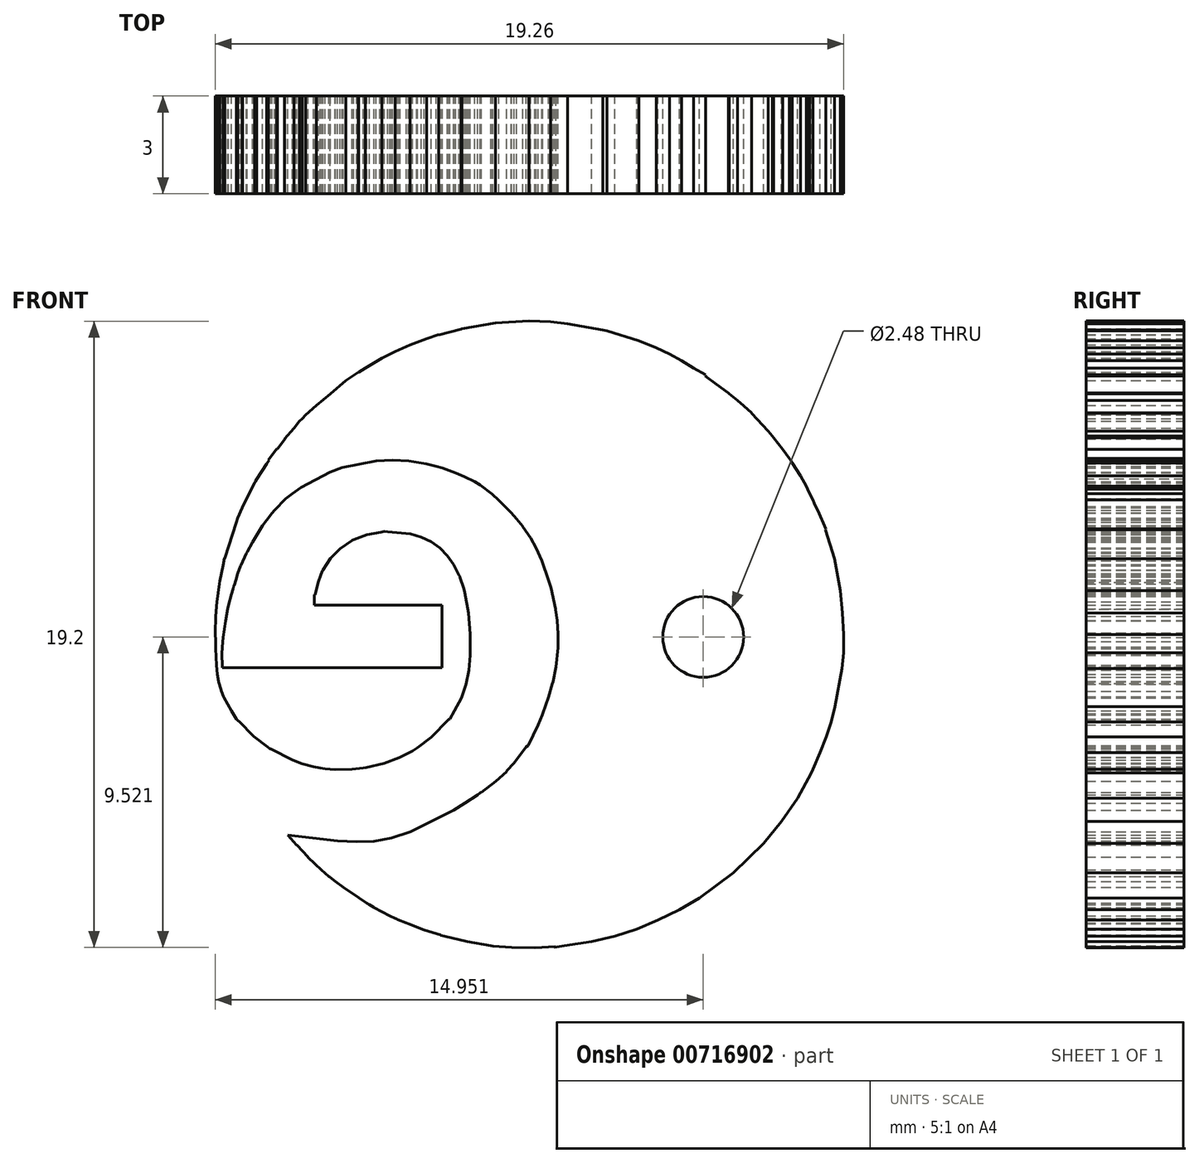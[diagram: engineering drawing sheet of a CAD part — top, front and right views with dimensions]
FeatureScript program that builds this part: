
annotation { "Feature Type Name" : "Feature", "Feature Type Description" : "" }
export const myFeature = defineFeature(function(context is Context, id is Id, definition is map)
    precondition{}
    {
        {
            var Q0;
            Q0=qCreatedBy(makeId("Front.planeOp"),FACE);
            var sketch = newSketch(context, id + "F0", { "sketchPlane" : qUnion([Q0])});
            skCircle(sketch, "E0", {"center": v(5.32, -0.08) * mm, "radius": 1.24 * mm});
            skLineSegment(sketch, "E1", {"start": v(7.48, 6.03) * mm, "end": v(7.76, 5.67) * mm});
            skLineSegment(sketch, "E2", {"start": v(7.76, 5.67) * mm, "end": v(7.96, 5.39) * mm});
            skLineSegment(sketch, "E3", {"start": v(7.44, 6.07) * mm, "end": v(7.48, 6.03) * mm});
            skLineSegment(sketch, "E4", {"start": v(7.44, 6.07) * mm, "end": v(7.44, 6.08) * mm});
            skLineSegment(sketch, "E5", {"start": v(7.44, 6.08) * mm, "end": v(7.3, 6.23) * mm});
            skLineSegment(sketch, "E6", {"start": v(6.8, 6.77) * mm, "end": v(7.3, 6.23) * mm});
            skLineSegment(sketch, "E7", {"start": v(6.8, 6.77) * mm, "end": v(6.8, 6.79) * mm});
            skLineSegment(sketch, "E8", {"start": v(6.8, 6.79) * mm, "end": v(6.57, 7) * mm});
            skLineSegment(sketch, "E9", {"start": v(6.12, 7.38) * mm, "end": v(6.37, 7.17) * mm});
            skLineSegment(sketch, "E10", {"start": v(6.37, 7.17) * mm, "end": v(6.57, 7) * mm});
            skLineSegment(sketch, "E11", {"start": v(6.1, 7.4) * mm, "end": v(6.12, 7.38) * mm});
            skLineSegment(sketch, "E12", {"start": v(6.1, 7.4) * mm, "end": v(6.1, 7.4) * mm});
            skLineSegment(sketch, "E13", {"start": v(6.1, 7.4) * mm, "end": v(5.72, 7.67) * mm});
            skLineSegment(sketch, "E14", {"start": v(5.39, 7.92) * mm, "end": v(5.72, 7.67) * mm});
            skLineSegment(sketch, "E15", {"start": v(5.39, 7.92) * mm, "end": v(5.4, 7.96) * mm});
            skLineSegment(sketch, "E16", {"start": v(5.4, 7.96) * mm, "end": v(5.03, 8.16) * mm});
            skLineSegment(sketch, "E17", {"start": v(4.66, 8.38) * mm, "end": v(5.03, 8.16) * mm});
            skLineSegment(sketch, "E18", {"start": v(4.66, 8.38) * mm, "end": v(4.66, 8.39) * mm});
            skLineSegment(sketch, "E19", {"start": v(4.66, 8.39) * mm, "end": v(4.3, 8.59) * mm});
            skLineSegment(sketch, "E20", {"start": v(4.3, 8.59) * mm, "end": v(4.3, 8.59) * mm});
            skLineSegment(sketch, "E21", {"start": v(3.35, 9) * mm, "end": v(3.88, 8.78) * mm});
            skLineSegment(sketch, "E22", {"start": v(3.88, 8.78) * mm, "end": v(4.3, 8.59) * mm});
            skLineSegment(sketch, "E23", {"start": v(2.37, 9.3) * mm, "end": v(3.35, 9) * mm});
            skLineSegment(sketch, "E24", {"start": v(2.37, 9.3) * mm, "end": v(2.37, 9.3) * mm});
            skLineSegment(sketch, "E25", {"start": v(2.37, 9.3) * mm, "end": v(2.25, 9.33) * mm});
            skLineSegment(sketch, "E26", {"start": v(1.17, 9.52) * mm, "end": v(2.25, 9.33) * mm});
            skLineSegment(sketch, "E27", {"start": v(-0.02, 9.6) * mm, "end": v(0.65, 9.58) * mm});
            skLineSegment(sketch, "E28", {"start": v(0.65, 9.58) * mm, "end": v(1.17, 9.52) * mm});
            skLineSegment(sketch, "E29", {"start": v(-2.07, 9.37) * mm, "end": v(-1.04, 9.55) * mm});
            skLineSegment(sketch, "E30", {"start": v(-1.04, 9.55) * mm, "end": v(-0.02, 9.6) * mm});
            skLineSegment(sketch, "E31", {"start": v(-2.07, 9.37) * mm, "end": v(-2.07, 9.37) * mm});
            skLineSegment(sketch, "E32", {"start": v(-2.07, 9.37) * mm, "end": v(-2.1, 9.36) * mm});
            skLineSegment(sketch, "E33", {"start": v(-2.78, 9.18) * mm, "end": v(-2.1, 9.36) * mm});
            skLineSegment(sketch, "E34", {"start": v(-2.78, 9.18) * mm, "end": v(-2.78, 9.18) * mm});
            skLineSegment(sketch, "E35", {"start": v(-2.78, 9.18) * mm, "end": v(-3.15, 9.06) * mm});
            skLineSegment(sketch, "E36", {"start": v(-4.12, 8.67) * mm, "end": v(-3.66, 8.87) * mm});
            skLineSegment(sketch, "E37", {"start": v(-3.66, 8.87) * mm, "end": v(-3.15, 9.06) * mm});
            skLineSegment(sketch, "E38", {"start": v(-5.03, 8.16) * mm, "end": v(-4.53, 8.46) * mm});
            skLineSegment(sketch, "E39", {"start": v(-4.53, 8.46) * mm, "end": v(-4.12, 8.67) * mm});
            skLineSegment(sketch, "E40", {"start": v(-5.03, 8.16) * mm, "end": v(-5.24, 8.04) * mm});
            skLineSegment(sketch, "E41", {"start": v(-5.24, 8.04) * mm, "end": v(-5.24, 8.03) * mm});
            skLineSegment(sketch, "E42", {"start": v(-5.62, 7.77) * mm, "end": v(-5.24, 8.03) * mm});
            skLineSegment(sketch, "E43", {"start": v(-5.62, 7.77) * mm, "end": v(-6.1, 7.38) * mm});
            skLineSegment(sketch, "E44", {"start": v(-6.1, 7.38) * mm, "end": v(-6.53, 7.02) * mm});
            skLineSegment(sketch, "E45", {"start": v(-6.53, 7.02) * mm, "end": v(-6.86, 6.72) * mm});
            skLineSegment(sketch, "E46", {"start": v(-6.86, 6.72) * mm, "end": v(-6.97, 6.62) * mm});
            skLineSegment(sketch, "E47", {"start": v(-6.97, 6.62) * mm, "end": v(-7.05, 6.53) * mm});
            skLineSegment(sketch, "E48", {"start": v(-7.05, 6.53) * mm, "end": v(-7.22, 6.32) * mm});
            skLineSegment(sketch, "E49", {"start": v(-7.22, 6.32) * mm, "end": v(-7.5, 6) * mm});
            skLineSegment(sketch, "E50", {"start": v(-7.5, 6) * mm, "end": v(-7.48, 6) * mm});
            skLineSegment(sketch, "E51", {"start": v(-7.48, 6) * mm, "end": v(-7.72, 5.69) * mm});
            skLineSegment(sketch, "E52", {"start": v(-7.72, 5.69) * mm, "end": v(-7.75, 5.69) * mm});
            skLineSegment(sketch, "E53", {"start": v(-7.75, 5.69) * mm, "end": v(-8, 5.34) * mm});
            skLineSegment(sketch, "E54", {"start": v(-8, 5.34) * mm, "end": v(-7.97, 5.34) * mm});
            skLineSegment(sketch, "E55", {"start": v(-7.97, 5.34) * mm, "end": v(-8, 5.3) * mm});
            skLineSegment(sketch, "E56", {"start": v(-8, 5.3) * mm, "end": v(-8.05, 5.23) * mm});
            skLineSegment(sketch, "E57", {"start": v(-8.05, 5.23) * mm, "end": v(-8.36, 4.75) * mm});
            skLineSegment(sketch, "E58", {"start": v(-8.36, 4.75) * mm, "end": v(-8.4, 4.69) * mm});
            skLineSegment(sketch, "E59", {"start": v(-8.4, 4.69) * mm, "end": v(-8.42, 4.64) * mm});
            skLineSegment(sketch, "E60", {"start": v(-8.42, 4.64) * mm, "end": v(-8.42, 4.64) * mm});
            skLineSegment(sketch, "E61", {"start": v(-8.42, 4.64) * mm, "end": v(-8.78, 3.92) * mm});
            skLineSegment(sketch, "E62", {"start": v(-8.78, 3.92) * mm, "end": v(-8.79, 3.92) * mm});
            skLineSegment(sketch, "E63", {"start": v(-8.79, 3.92) * mm, "end": v(-8.8, 3.89) * mm});
            skLineSegment(sketch, "E64", {"start": v(-8.8, 3.89) * mm, "end": v(-8.94, 3.56) * mm});
            skLineSegment(sketch, "E65", {"start": v(-8.94, 3.56) * mm, "end": v(-8.98, 3.44) * mm});
            skLineSegment(sketch, "E66", {"start": v(-8.98, 3.44) * mm, "end": v(-9.33, 2.33) * mm});
            skLineSegment(sketch, "E67", {"start": v(-9.33, 2.33) * mm, "end": v(-9.35, 2.33) * mm});
            skLineSegment(sketch, "E68", {"start": v(-9.35, 2.33) * mm, "end": v(-9.38, 2.11) * mm});
            skLineSegment(sketch, "E69", {"start": v(-9.38, 2.11) * mm, "end": v(-9.48, 1.64) * mm});
            skLineSegment(sketch, "E70", {"start": v(-9.48, 1.64) * mm, "end": v(-9.49, 1.64) * mm});
            skLineSegment(sketch, "E71", {"start": v(-9.49, 1.64) * mm, "end": v(-9.5, 1.55) * mm});
            skLineSegment(sketch, "E72", {"start": v(-9.5, 1.55) * mm, "end": v(-9.58, 1) * mm});
            skLineSegment(sketch, "E73", {"start": v(-9.58, 1) * mm, "end": v(-9.61, 0.55) * mm});
            skLineSegment(sketch, "E74", {"start": v(-9.61, 0.55) * mm, "end": v(-9.63, 0.05) * mm});
            skLineSegment(sketch, "E75", {"start": v(-9.63, 0.05) * mm, "end": v(-9.62, -0.23) * mm});
            skLineSegment(sketch, "E76", {"start": v(-9.62, -0.23) * mm, "end": v(-9.62, -0.44) * mm});
            skLineSegment(sketch, "E77", {"start": v(-9.62, -0.44) * mm, "end": v(-9.62, -0.44) * mm});
            skLineSegment(sketch, "E78", {"start": v(-9.62, -0.44) * mm, "end": v(-9.6, -0.94) * mm});
            skLineSegment(sketch, "E79", {"start": v(-9.6, -0.94) * mm, "end": v(-9.57, -1.23) * mm});
            skLineSegment(sketch, "E80", {"start": v(-9.57, -1.23) * mm, "end": v(-9.53, -1.45) * mm});
            skLineSegment(sketch, "E81", {"start": v(-9.53, -1.45) * mm, "end": v(-9.53, -1.45) * mm});
            skLineSegment(sketch, "E82", {"start": v(-9.53, -1.45) * mm, "end": v(-9.5, -1.53) * mm});
            skLineSegment(sketch, "E83", {"start": v(-9.5, -1.53) * mm, "end": v(-9.44, -1.74) * mm});
            skLineSegment(sketch, "E84", {"start": v(-9.44, -1.74) * mm, "end": v(-9.37, -1.9) * mm});
            skLineSegment(sketch, "E85", {"start": v(-9.37, -1.9) * mm, "end": v(-9.36, -1.93) * mm});
            skLineSegment(sketch, "E86", {"start": v(-9.36, -1.93) * mm, "end": v(-9.13, -2.35) * mm});
            skLineSegment(sketch, "E87", {"start": v(-9.13, -2.35) * mm, "end": v(-8.98, -2.6) * mm});
            skLineSegment(sketch, "E88", {"start": v(-8.98, -2.6) * mm, "end": v(-8.92, -2.66) * mm});
            skLineSegment(sketch, "E89", {"start": v(-8.92, -2.66) * mm, "end": v(-8.9, -2.66) * mm});
            skLineSegment(sketch, "E90", {"start": v(-8.9, -2.66) * mm, "end": v(-8.45, -3.14) * mm});
            skLineSegment(sketch, "E91", {"start": v(-8.45, -3.14) * mm, "end": v(-8.03, -3.45) * mm});
            skLineSegment(sketch, "E92", {"start": v(-8.03, -3.45) * mm, "end": v(-7.96, -3.5) * mm});
            skLineSegment(sketch, "E93", {"start": v(-7.96, -3.5) * mm, "end": v(-7.94, -3.51) * mm});
            skLineSegment(sketch, "E94", {"start": v(-7.94, -3.51) * mm, "end": v(-7.93, -3.51) * mm});
            skLineSegment(sketch, "E95", {"start": v(-7.93, -3.51) * mm, "end": v(-7.26, -3.86) * mm});
            skLineSegment(sketch, "E96", {"start": v(-7.26, -3.86) * mm, "end": v(-6.96, -3.97) * mm});
            skLineSegment(sketch, "E97", {"start": v(-6.96, -3.97) * mm, "end": v(-6.62, -4.06) * mm});
            skLineSegment(sketch, "E98", {"start": v(-6.62, -4.06) * mm, "end": v(-6.41, -4.1) * mm});
            skLineSegment(sketch, "E99", {"start": v(-6.41, -4.1) * mm, "end": v(-6.26, -4.12) * mm});
            skLineSegment(sketch, "E100", {"start": v(-6.26, -4.12) * mm, "end": v(-5.96, -4.15) * mm});
            skLineSegment(sketch, "E101", {"start": v(-5.96, -4.15) * mm, "end": v(-5.44, -4.14) * mm});
            skLineSegment(sketch, "E102", {"start": v(-5.44, -4.14) * mm, "end": v(-5.1, -4.1) * mm});
            skLineSegment(sketch, "E103", {"start": v(-5.1, -4.1) * mm, "end": v(-5, -4.08) * mm});
            skLineSegment(sketch, "E104", {"start": v(-5, -4.08) * mm, "end": v(-4.46, -3.96) * mm});
            skLineSegment(sketch, "E105", {"start": v(-4.46, -3.96) * mm, "end": v(-3.99, -3.78) * mm});
            skLineSegment(sketch, "E106", {"start": v(-3.99, -3.78) * mm, "end": v(-3.96, -3.77) * mm});
            skLineSegment(sketch, "E107", {"start": v(-3.96, -3.77) * mm, "end": v(-3.61, -3.6) * mm});
            skLineSegment(sketch, "E108", {"start": v(-3.61, -3.6) * mm, "end": v(-3.59, -3.58) * mm});
            skLineSegment(sketch, "E109", {"start": v(-3.59, -3.58) * mm, "end": v(-3.43, -3.48) * mm});
            skLineSegment(sketch, "E110", {"start": v(-3.43, -3.48) * mm, "end": v(-3, -3.16) * mm});
            skLineSegment(sketch, "E111", {"start": v(-3, -3.16) * mm, "end": v(-2.48, -2.6) * mm});
            skLineSegment(sketch, "E112", {"start": v(-2.48, -2.6) * mm, "end": v(-2.44, -2.6) * mm});
            skLineSegment(sketch, "E113", {"start": v(-2.44, -2.6) * mm, "end": v(-2.3, -2.35) * mm});
            skLineSegment(sketch, "E114", {"start": v(-2.3, -2.35) * mm, "end": v(-2.08, -1.95) * mm});
            skLineSegment(sketch, "E115", {"start": v(-2.08, -1.95) * mm, "end": v(-1.94, -1.53) * mm});
            skLineSegment(sketch, "E116", {"start": v(-1.94, -1.53) * mm, "end": v(-1.86, -1.1) * mm});
            skLineSegment(sketch, "E117", {"start": v(-1.86, -1.1) * mm, "end": v(-1.82, -0.64) * mm});
            skLineSegment(sketch, "E118", {"start": v(-1.82, -0.64) * mm, "end": v(-1.81, 0) * mm});
            skLineSegment(sketch, "E119", {"start": v(-1.81, 0) * mm, "end": v(-1.86, 0.65) * mm});
            skLineSegment(sketch, "E120", {"start": v(-1.86, 0.65) * mm, "end": v(-1.98, 1.28) * mm});
            skLineSegment(sketch, "E121", {"start": v(-1.98, 1.28) * mm, "end": v(-2, 1.4) * mm});
            skLineSegment(sketch, "E122", {"start": v(-2, 1.4) * mm, "end": v(-2.01, 1.39) * mm});
            skLineSegment(sketch, "E123", {"start": v(-2.01, 1.39) * mm, "end": v(-2.13, 1.76) * mm});
            skLineSegment(sketch, "E124", {"start": v(-2.13, 1.76) * mm, "end": v(-2.13, 1.76) * mm});
            skLineSegment(sketch, "E125", {"start": v(-2.13, 1.76) * mm, "end": v(-2.16, 1.81) * mm});
            skLineSegment(sketch, "E126", {"start": v(-2.16, 1.81) * mm, "end": v(-2.32, 2.14) * mm});
            skLineSegment(sketch, "E127", {"start": v(-2.32, 2.14) * mm, "end": v(-2.51, 2.41) * mm});
            skLineSegment(sketch, "E128", {"start": v(-2.51, 2.41) * mm, "end": v(-2.74, 2.65) * mm});
            skLineSegment(sketch, "E129", {"start": v(-2.74, 2.65) * mm, "end": v(-3.01, 2.84) * mm});
            skLineSegment(sketch, "E130", {"start": v(-3.01, 2.84) * mm, "end": v(-3.3, 2.98) * mm});
            skLineSegment(sketch, "E131", {"start": v(-3.3, 2.98) * mm, "end": v(-3.64, 3.08) * mm});
            skLineSegment(sketch, "E132", {"start": v(-3.64, 3.08) * mm, "end": v(-4.35, 3.15) * mm});
            skLineSegment(sketch, "E133", {"start": v(-4.35, 3.15) * mm, "end": v(-4.45, 3.15) * mm});
            skLineSegment(sketch, "E134", {"start": v(-4.45, 3.15) * mm, "end": v(-4.55, 3.14) * mm});
            skLineSegment(sketch, "E135", {"start": v(-4.55, 3.14) * mm, "end": v(-4.99, 3.05) * mm});
            skLineSegment(sketch, "E136", {"start": v(-4.99, 3.05) * mm, "end": v(-5.39, 2.9) * mm});
            skLineSegment(sketch, "E137", {"start": v(-5.39, 2.9) * mm, "end": v(-5.42, 2.89) * mm});
            skLineSegment(sketch, "E138", {"start": v(-5.42, 2.89) * mm, "end": v(-5.44, 2.87) * mm});
            skLineSegment(sketch, "E139", {"start": v(-5.44, 2.87) * mm, "end": v(-5.8, 2.62) * mm});
            skLineSegment(sketch, "E140", {"start": v(-5.8, 2.62) * mm, "end": v(-6.1, 2.33) * mm});
            skLineSegment(sketch, "E141", {"start": v(-6.1, 2.33) * mm, "end": v(-6.32, 1.97) * mm});
            skLineSegment(sketch, "E142", {"start": v(-6.32, 1.97) * mm, "end": v(-6.34, 1.97) * mm});
            skLineSegment(sketch, "E143", {"start": v(-6.34, 1.97) * mm, "end": v(-6.39, 1.84) * mm});
            skLineSegment(sketch, "E144", {"start": v(-6.39, 1.84) * mm, "end": v(-6.48, 1.58) * mm});
            skLineSegment(sketch, "E145", {"start": v(-6.48, 1.58) * mm, "end": v(-6.48, 1.58) * mm});
            skLineSegment(sketch, "E146", {"start": v(-6.48, 1.58) * mm, "end": v(-6.56, 1.21) * mm});
            skLineSegment(sketch, "E147", {"start": v(-6.56, 1.21) * mm, "end": v(-6.59, 1.2) * mm});
            skLineSegment(sketch, "E148", {"start": v(-6.59, 1.2) * mm, "end": v(-6.59, 0.9) * mm});
            skLineSegment(sketch, "E149", {"start": v(-6.59, 0.9) * mm, "end": v(-2.68, 0.9) * mm});
            skLineSegment(sketch, "E150", {"start": v(-2.68, 0.9) * mm, "end": v(-2.68, -1.02) * mm});
            skLineSegment(sketch, "E151", {"start": v(-2.87, -1.02) * mm, "end": v(-2.68, -1.02) * mm});
            skLineSegment(sketch, "E152", {"start": v(-2.87, -1.02) * mm, "end": v(-3.46, -1.02) * mm});
            skLineSegment(sketch, "E153", {"start": v(-3.46, -1.02) * mm, "end": v(-3.46, -1.02) * mm});
            skLineSegment(sketch, "E154", {"start": v(-4.59, -1.02) * mm, "end": v(-3.46, -1.02) * mm});
            skLineSegment(sketch, "E155", {"start": v(-4.59, -1.02) * mm, "end": v(-4.58, -1.02) * mm});
            skLineSegment(sketch, "E156", {"start": v(-4.58, -1.02) * mm, "end": v(-9.4, -1.02) * mm});
            skLineSegment(sketch, "E157", {"start": v(-9.4, -0.98) * mm, "end": v(-9.43, -0.6) * mm});
            skLineSegment(sketch, "E158", {"start": v(-9.38, -0.1) * mm, "end": v(-9.41, -0.38) * mm});
            skLineSegment(sketch, "E159", {"start": v(-9.41, -0.38) * mm, "end": v(-9.43, -0.6) * mm});
            skLineSegment(sketch, "E160", {"start": v(-9.31, 0.41) * mm, "end": v(-9.38, -0.1) * mm});
            skLineSegment(sketch, "E161", {"start": v(-9.31, 0.41) * mm, "end": v(-9.3, 0.41) * mm});
            skLineSegment(sketch, "E162", {"start": v(-9.3, 0.41) * mm, "end": v(-9.24, 0.78) * mm});
            skLineSegment(sketch, "E163", {"start": v(-9.22, 0.9) * mm, "end": v(-9.24, 0.78) * mm});
            skLineSegment(sketch, "E164", {"start": v(-9.13, 1.23) * mm, "end": v(-9.22, 0.9) * mm});
            skLineSegment(sketch, "E165", {"start": v(-9.09, 1.39) * mm, "end": v(-9.13, 1.23) * mm});
            skLineSegment(sketch, "E166", {"start": v(-9.08, 1.41) * mm, "end": v(-9.09, 1.39) * mm});
            skLineSegment(sketch, "E167", {"start": v(-9.07, 1.43) * mm, "end": v(-9.08, 1.41) * mm});
            skLineSegment(sketch, "E168", {"start": v(-9.05, 1.5) * mm, "end": v(-9.07, 1.43) * mm});
            skLineSegment(sketch, "E169", {"start": v(-9.05, 1.5) * mm, "end": v(-9.05, 1.5) * mm});
            skLineSegment(sketch, "E170", {"start": v(-9, 1.67) * mm, "end": v(-9.05, 1.5) * mm});
            skLineSegment(sketch, "E171", {"start": v(-8.85, 2.1) * mm, "end": v(-8.94, 1.86) * mm});
            skLineSegment(sketch, "E172", {"start": v(-8.94, 1.86) * mm, "end": v(-9, 1.67) * mm});
            skLineSegment(sketch, "E173", {"start": v(-8.85, 2.11) * mm, "end": v(-8.85, 2.1) * mm});
            skLineSegment(sketch, "E174", {"start": v(-8.68, 2.48) * mm, "end": v(-8.85, 2.11) * mm});
            skLineSegment(sketch, "E175", {"start": v(-8.66, 2.52) * mm, "end": v(-8.68, 2.48) * mm});
            skLineSegment(sketch, "E176", {"start": v(-8.66, 2.52) * mm, "end": v(-8.49, 2.82) * mm});
            skLineSegment(sketch, "E177", {"start": v(-8.17, 3.33) * mm, "end": v(-8.49, 2.82) * mm});
            skLineSegment(sketch, "E178", {"start": v(-7.89, 3.72) * mm, "end": v(-8.05, 3.5) * mm});
            skLineSegment(sketch, "E179", {"start": v(-8.05, 3.5) * mm, "end": v(-8.17, 3.33) * mm});
            skLineSegment(sketch, "E180", {"start": v(-7.82, 3.8) * mm, "end": v(-7.89, 3.72) * mm});
            skLineSegment(sketch, "E181", {"start": v(-7.82, 3.8) * mm, "end": v(-7.81, 3.8) * mm});
            skLineSegment(sketch, "E182", {"start": v(-7.81, 3.8) * mm, "end": v(-7.47, 4.15) * mm});
            skLineSegment(sketch, "E183", {"start": v(-7, 4.5) * mm, "end": v(-7.26, 4.31) * mm});
            skLineSegment(sketch, "E184", {"start": v(-7.26, 4.31) * mm, "end": v(-7.47, 4.15) * mm});
            skLineSegment(sketch, "E185", {"start": v(-7, 4.5) * mm, "end": v(-6.12, 4.97) * mm});
            skLineSegment(sketch, "E186", {"start": v(-5.74, 5.1) * mm, "end": v(-6.12, 4.97) * mm});
            skLineSegment(sketch, "E187", {"start": v(-5.74, 5.1) * mm, "end": v(-4.7, 5.32) * mm});
            skLineSegment(sketch, "E188", {"start": v(-4.2, 5.35) * mm, "end": v(-4.7, 5.32) * mm});
            skLineSegment(sketch, "E189", {"start": v(-4.2, 5.35) * mm, "end": v(-4.2, 5.34) * mm});
            skLineSegment(sketch, "E190", {"start": v(-4.2, 5.34) * mm, "end": v(-3.7, 5.32) * mm});
            skLineSegment(sketch, "E191", {"start": v(-3.17, 5.23) * mm, "end": v(-3.7, 5.32) * mm});
            skLineSegment(sketch, "E192", {"start": v(-3.17, 5.23) * mm, "end": v(-2.86, 5.15) * mm});
            skLineSegment(sketch, "E193", {"start": v(-2.26, 4.95) * mm, "end": v(-2.66, 5.1) * mm});
            skLineSegment(sketch, "E194", {"start": v(-2.66, 5.1) * mm, "end": v(-2.86, 5.15) * mm});
            skLineSegment(sketch, "E195", {"start": v(-1.67, 4.68) * mm, "end": v(-2, 4.84) * mm});
            skLineSegment(sketch, "E196", {"start": v(-2, 4.84) * mm, "end": v(-2.26, 4.95) * mm});
            skLineSegment(sketch, "E197", {"start": v(-1.67, 4.68) * mm, "end": v(-1.51, 4.58) * mm});
            skLineSegment(sketch, "E198", {"start": v(-1.14, 4.3) * mm, "end": v(-1.51, 4.58) * mm});
            skLineSegment(sketch, "E199", {"start": v(-1.14, 4.3) * mm, "end": v(-0.94, 4.11) * mm});
            skLineSegment(sketch, "E200", {"start": v(-0.56, 3.72) * mm, "end": v(-0.94, 4.11) * mm});
            skLineSegment(sketch, "E201", {"start": v(-0.2, 3.3) * mm, "end": v(-0.4, 3.54) * mm});
            skLineSegment(sketch, "E202", {"start": v(-0.4, 3.54) * mm, "end": v(-0.56, 3.72) * mm});
            skLineSegment(sketch, "E203", {"start": v(-0.2, 3.3) * mm, "end": v(-0.2, 3.3) * mm});
            skLineSegment(sketch, "E204", {"start": v(-0.2, 3.3) * mm, "end": v(0.04, 2.95) * mm});
            skLineSegment(sketch, "E205", {"start": v(0.38, 2.25) * mm, "end": v(0.2, 2.65) * mm});
            skLineSegment(sketch, "E206", {"start": v(0.2, 2.65) * mm, "end": v(0.04, 2.95) * mm});
            skLineSegment(sketch, "E207", {"start": v(0.59, 1.66) * mm, "end": v(0.38, 2.25) * mm});
            skLineSegment(sketch, "E208", {"start": v(0.65, 1.43) * mm, "end": v(0.59, 1.66) * mm});
            skLineSegment(sketch, "E209", {"start": v(0.8, 0.78) * mm, "end": v(0.65, 1.43) * mm});
            skLineSegment(sketch, "E210", {"start": v(0.8, 0.78) * mm, "end": v(0.8, 0.78) * mm});
            skLineSegment(sketch, "E211", {"start": v(0.8, 0.75) * mm, "end": v(0.8, 0.78) * mm});
            skLineSegment(sketch, "E212", {"start": v(0.88, 0.01) * mm, "end": v(0.84, 0.43) * mm});
            skLineSegment(sketch, "E213", {"start": v(0.84, 0.43) * mm, "end": v(0.8, 0.75) * mm});
            skLineSegment(sketch, "E214", {"start": v(0.88, 0.01) * mm, "end": v(0.88, -0.41) * mm});
            skLineSegment(sketch, "E215", {"start": v(0.82, -1) * mm, "end": v(0.88, -0.41) * mm});
            skLineSegment(sketch, "E216", {"start": v(0.82, -1) * mm, "end": v(0.72, -1.45) * mm});
            skLineSegment(sketch, "E217", {"start": v(0.7, -1.52) * mm, "end": v(0.72, -1.45) * mm});
            skLineSegment(sketch, "E218", {"start": v(0.4, -2.43) * mm, "end": v(0.58, -1.93) * mm});
            skLineSegment(sketch, "E219", {"start": v(0.58, -1.93) * mm, "end": v(0.7, -1.52) * mm});
            skLineSegment(sketch, "E220", {"start": v(0.4, -2.46) * mm, "end": v(0.4, -2.43) * mm});
            skLineSegment(sketch, "E221", {"start": v(0.4, -2.46) * mm, "end": v(0.26, -2.78) * mm});
            skLineSegment(sketch, "E222", {"start": v(-0.04, -3.4) * mm, "end": v(0.26, -2.78) * mm});
            skLineSegment(sketch, "E223", {"start": v(-0.04, -3.4) * mm, "end": v(-0.1, -3.45) * mm});
            skLineSegment(sketch, "E224", {"start": v(-0.1, -3.45) * mm, "end": v(-0.47, -3.94) * mm});
            skLineSegment(sketch, "E225", {"start": v(-0.47, -3.94) * mm, "end": v(-0.7, -4.2) * mm});
            skLineSegment(sketch, "E226", {"start": v(-0.7, -4.2) * mm, "end": v(-0.7, -4.21) * mm});
            skLineSegment(sketch, "E227", {"start": v(-1.48, -4.84) * mm, "end": v(-1.03, -4.5) * mm});
            skLineSegment(sketch, "E228", {"start": v(-1.03, -4.5) * mm, "end": v(-0.7, -4.21) * mm});
            skLineSegment(sketch, "E229", {"start": v(-1.49, -4.84) * mm, "end": v(-1.48, -4.84) * mm});
            skLineSegment(sketch, "E230", {"start": v(-1.5, -4.86) * mm, "end": v(-1.49, -4.84) * mm});
            skLineSegment(sketch, "E231", {"start": v(-1.51, -4.86) * mm, "end": v(-1.5, -4.86) * mm});
            skLineSegment(sketch, "E232", {"start": v(-1.6, -4.92) * mm, "end": v(-1.51, -4.86) * mm});
            skLineSegment(sketch, "E233", {"start": v(-1.99, -5.18) * mm, "end": v(-1.6, -4.92) * mm});
            skLineSegment(sketch, "E234", {"start": v(-2.33, -5.39) * mm, "end": v(-1.99, -5.18) * mm});
            skLineSegment(sketch, "E235", {"start": v(-2.33, -5.39) * mm, "end": v(-3.64, -6.05) * mm});
            skLineSegment(sketch, "E236", {"start": v(-5.88, -6.33) * mm, "end": v(-5.3, -6.36) * mm});
            skLineSegment(sketch, "E237", {"start": v(-5.3, -6.36) * mm, "end": v(-4.77, -6.34) * mm});
            skLineSegment(sketch, "E238", {"start": v(-4.77, -6.34) * mm, "end": v(-4.23, -6.25) * mm});
            skLineSegment(sketch, "E239", {"start": v(-4.23, -6.25) * mm, "end": v(-3.64, -6.05) * mm});
            skLineSegment(sketch, "E240", {"start": v(-5.88, -6.33) * mm, "end": v(-7.4, -6.15) * mm});
            skLineSegment(sketch, "E241", {"start": v(-7.4, -6.15) * mm, "end": v(-7.14, -6.46) * mm});
            skLineSegment(sketch, "E242", {"start": v(-7.14, -6.46) * mm, "end": v(-7.13, -6.46) * mm});
            skLineSegment(sketch, "E243", {"start": v(-6.78, -6.83) * mm, "end": v(-7.13, -6.46) * mm});
            skLineSegment(sketch, "E244", {"start": v(-6.78, -6.83) * mm, "end": v(-6.8, -6.83) * mm});
            skLineSegment(sketch, "E245", {"start": v(-6.8, -6.83) * mm, "end": v(-6.56, -7.04) * mm});
            skLineSegment(sketch, "E246", {"start": v(-6.14, -7.42) * mm, "end": v(-6.38, -7.22) * mm});
            skLineSegment(sketch, "E247", {"start": v(-6.38, -7.22) * mm, "end": v(-6.56, -7.04) * mm});
            skLineSegment(sketch, "E248", {"start": v(-6.12, -7.44) * mm, "end": v(-6.14, -7.42) * mm});
            skLineSegment(sketch, "E249", {"start": v(-5.7, -7.76) * mm, "end": v(-5.94, -7.58) * mm});
            skLineSegment(sketch, "E250", {"start": v(-5.94, -7.58) * mm, "end": v(-6.13, -7.44) * mm});
            skLineSegment(sketch, "E251", {"start": v(-5.24, -8.08) * mm, "end": v(-5.7, -7.76) * mm});
            skLineSegment(sketch, "E252", {"start": v(-4.99, -8.24) * mm, "end": v(-5.24, -8.08) * mm});
            skLineSegment(sketch, "E253", {"start": v(-4.9, -8.29) * mm, "end": v(-4.99, -8.24) * mm});
            skLineSegment(sketch, "E254", {"start": v(-4.78, -8.36) * mm, "end": v(-4.9, -8.29) * mm});
            skLineSegment(sketch, "E255", {"start": v(-4.76, -8.37) * mm, "end": v(-4.78, -8.36) * mm});
            skLineSegment(sketch, "E256", {"start": v(-4.28, -8.63) * mm, "end": v(-4.76, -8.37) * mm});
            skLineSegment(sketch, "E257", {"start": v(-4.12, -8.7) * mm, "end": v(-4.28, -8.63) * mm});
            skLineSegment(sketch, "E258", {"start": v(-4.08, -8.72) * mm, "end": v(-4.12, -8.7) * mm});
            skLineSegment(sketch, "E259", {"start": v(-4.04, -8.74) * mm, "end": v(-4.08, -8.72) * mm});
            skLineSegment(sketch, "E260", {"start": v(-3.77, -8.85) * mm, "end": v(-4.04, -8.74) * mm});
            skLineSegment(sketch, "E261", {"start": v(-3.71, -8.88) * mm, "end": v(-3.77, -8.85) * mm});
            skLineSegment(sketch, "E262", {"start": v(-2.71, -9.22) * mm, "end": v(-3.23, -9.06) * mm});
            skLineSegment(sketch, "E263", {"start": v(-3.23, -9.06) * mm, "end": v(-3.71, -8.88) * mm});
            skLineSegment(sketch, "E264", {"start": v(-2.71, -9.22) * mm, "end": v(-2.72, -9.22) * mm});
            skLineSegment(sketch, "E265", {"start": v(-2.72, -9.22) * mm, "end": v(-2.6, -9.25) * mm});
            skLineSegment(sketch, "E266", {"start": v(-1.18, -9.54) * mm, "end": v(-1.9, -9.42) * mm});
            skLineSegment(sketch, "E267", {"start": v(-1.9, -9.42) * mm, "end": v(-2.6, -9.25) * mm});
            skLineSegment(sketch, "E268", {"start": v(-1.18, -9.54) * mm, "end": v(-1.19, -9.55) * mm});
            skLineSegment(sketch, "E269", {"start": v(-1.19, -9.55) * mm, "end": v(-1.11, -9.55) * mm});
            skLineSegment(sketch, "E270", {"start": v(0.17, -9.6) * mm, "end": v(-0.55, -9.6) * mm});
            skLineSegment(sketch, "E271", {"start": v(-0.55, -9.6) * mm, "end": v(-1.11, -9.55) * mm});
            skLineSegment(sketch, "E272", {"start": v(0.8, -9.57) * mm, "end": v(0.17, -9.6) * mm});
            skLineSegment(sketch, "E273", {"start": v(0.8, -9.57) * mm, "end": v(0.76, -9.59) * mm});
            skLineSegment(sketch, "E274", {"start": v(0.76, -9.59) * mm, "end": v(1.07, -9.54) * mm});
            skLineSegment(sketch, "E275", {"start": v(5.2, -8.09) * mm, "end": v(4.6, -8.44) * mm});
            skLineSegment(sketch, "E276", {"start": v(4.6, -8.44) * mm, "end": v(3.94, -8.76) * mm});
            skLineSegment(sketch, "E277", {"start": v(3.94, -8.76) * mm, "end": v(3.29, -9.03) * mm});
            skLineSegment(sketch, "E278", {"start": v(3.29, -9.03) * mm, "end": v(2.61, -9.25) * mm});
            skLineSegment(sketch, "E279", {"start": v(2.61, -9.25) * mm, "end": v(1.9, -9.42) * mm});
            skLineSegment(sketch, "E280", {"start": v(1.9, -9.42) * mm, "end": v(1.07, -9.54) * mm});
            skLineSegment(sketch, "E281", {"start": v(8.63, -4.25) * mm, "end": v(8.2, -5.02) * mm});
            skLineSegment(sketch, "E282", {"start": v(8.2, -5.02) * mm, "end": v(7.72, -5.73) * mm});
            skLineSegment(sketch, "E283", {"start": v(7.72, -5.73) * mm, "end": v(7.17, -6.4) * mm});
            skLineSegment(sketch, "E284", {"start": v(7.17, -6.4) * mm, "end": v(6.24, -7.31) * mm});
            skLineSegment(sketch, "E285", {"start": v(6.24, -7.31) * mm, "end": v(5.2, -8.09) * mm});
            skLineSegment(sketch, "E286", {"start": v(8.69, -4.13) * mm, "end": v(8.63, -4.25) * mm});
            skLineSegment(sketch, "E287", {"start": v(9.36, -2.22) * mm, "end": v(9.24, -2.68) * mm});
            skLineSegment(sketch, "E288", {"start": v(9.24, -2.68) * mm, "end": v(9.1, -3.14) * mm});
            skLineSegment(sketch, "E289", {"start": v(9.1, -3.14) * mm, "end": v(8.9, -3.63) * mm});
            skLineSegment(sketch, "E290", {"start": v(8.9, -3.63) * mm, "end": v(8.69, -4.13) * mm});
            skLineSegment(sketch, "E291", {"start": v(9.58, -1.05) * mm, "end": v(9.36, -2.22) * mm});
            skLineSegment(sketch, "E292", {"start": v(9.52, 1.34) * mm, "end": v(9.6, 0.66) * mm});
            skLineSegment(sketch, "E293", {"start": v(9.6, 0.66) * mm, "end": v(9.63, 0) * mm});
            skLineSegment(sketch, "E294", {"start": v(9.63, 0) * mm, "end": v(9.62, -0.56) * mm});
            skLineSegment(sketch, "E295", {"start": v(9.62, -0.56) * mm, "end": v(9.58, -1.05) * mm});
            skLineSegment(sketch, "E296", {"start": v(9.07, 3.21) * mm, "end": v(9.35, 2.31) * mm});
            skLineSegment(sketch, "E297", {"start": v(9.35, 2.31) * mm, "end": v(9.52, 1.34) * mm});
            skLineSegment(sketch, "E298", {"start": v(9.07, 3.21) * mm, "end": v(9.08, 3.23) * mm});
            skLineSegment(sketch, "E299", {"start": v(9.08, 3.23) * mm, "end": v(8.83, 3.79) * mm});
            skLineSegment(sketch, "E300", {"start": v(8.79, 3.88) * mm, "end": v(8.83, 3.79) * mm});
            skLineSegment(sketch, "E301", {"start": v(8.73, 4.02) * mm, "end": v(8.79, 3.88) * mm});
            skLineSegment(sketch, "E302", {"start": v(8.68, 4.12) * mm, "end": v(8.73, 4.02) * mm});
            skLineSegment(sketch, "E303", {"start": v(8.59, 4.32) * mm, "end": v(8.68, 4.12) * mm});
            skLineSegment(sketch, "E304", {"start": v(8.52, 4.45) * mm, "end": v(8.59, 4.32) * mm});
            skLineSegment(sketch, "E305", {"start": v(8.48, 4.54) * mm, "end": v(8.52, 4.45) * mm});
            skLineSegment(sketch, "E306", {"start": v(8.05, 5.25) * mm, "end": v(8.3, 4.86) * mm});
            skLineSegment(sketch, "E307", {"start": v(8.3, 4.86) * mm, "end": v(8.48, 4.54) * mm});
            skLineSegment(sketch, "E308", {"start": v(8.05, 5.25) * mm, "end": v(8.06, 5.26) * mm});
            skLineSegment(sketch, "E309", {"start": v(8.06, 5.26) * mm, "end": v(8, 5.34) * mm});
            skLineSegment(sketch, "E310", {"start": v(7.96, 5.39) * mm, "end": v(8, 5.34) * mm});
            skLineSegment(sketch, "E311", {"start": v(-9.4, -0.98) * mm, "end": v(-9.4, -1.02) * mm});
            skSolve(sketch);
        }
        {
            var Q0;
            Q0 = qSketchRegion(id + "F0", true);
            extrude(context, id + "F1", {"entities" : qUnion([Q0]), "depth" : 3 * mm, "offsetDistance" : 25.4 * mm});
        }
    });
